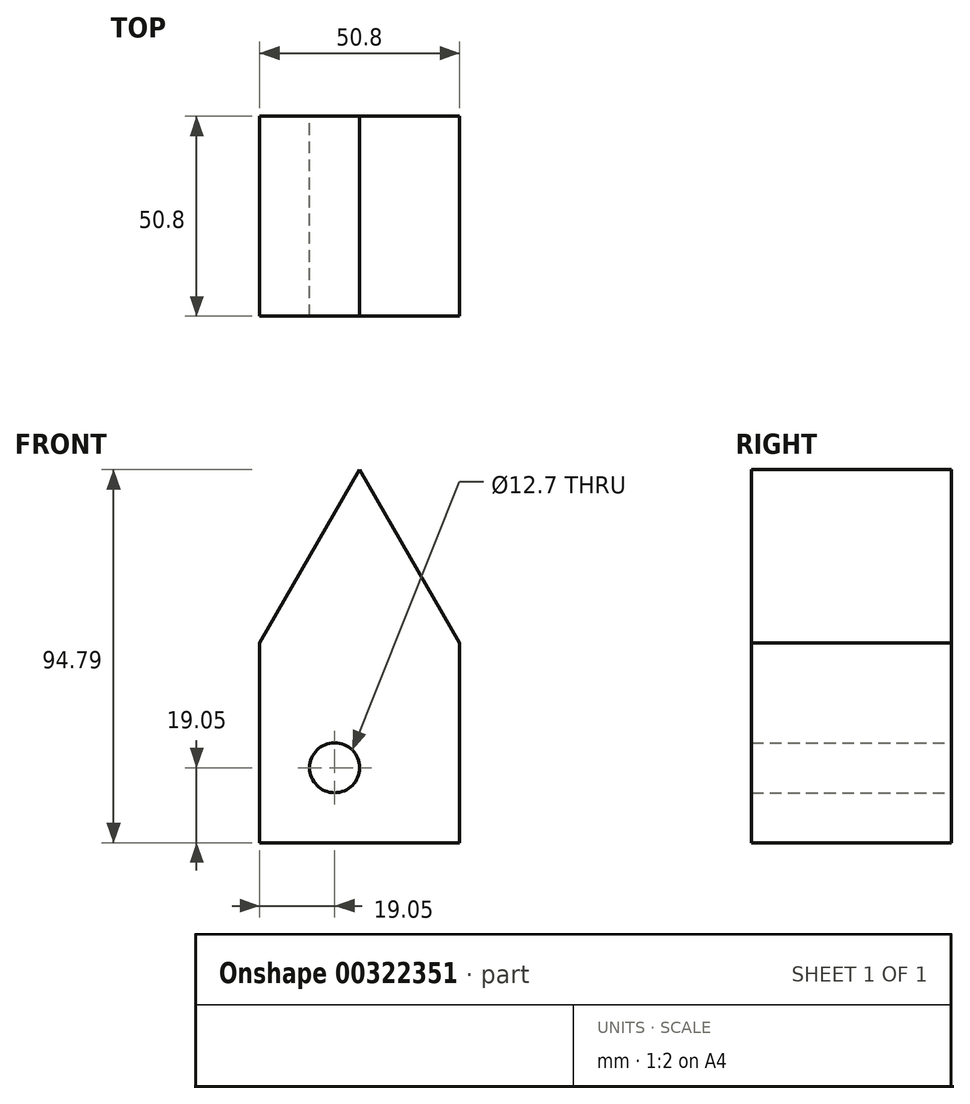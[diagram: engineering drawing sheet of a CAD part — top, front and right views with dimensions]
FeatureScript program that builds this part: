
annotation { "Feature Type Name" : "Feature", "Feature Type Description" : "" }
export const myFeature = defineFeature(function(context is Context, id is Id, definition is map)
    precondition{}
    {
        {
            var Q0;
            Q0=qCreatedBy(makeId("Front.planeOp"),FACE);
            var sketch = newSketch(context, id + "F0", { "sketchPlane" : qUnion([Q0])});
            skLineSegment(sketch, "E0.bottom", {"start": v(25.4, 25.4) * mm, "end": v(-25.4, 25.4) * mm});
            skLineSegment(sketch, "E0.top", {"start": v(25.4, -25.4) * mm, "end": v(-25.4, -25.4) * mm});
            skLineSegment(sketch, "E0.left", {"start": v(25.4, 25.4) * mm, "end": v(25.4, -25.4) * mm});
            skLineSegment(sketch, "E0.right", {"start": v(-25.4, 25.4) * mm, "end": v(-25.4, -25.4) * mm});
            skPoint(sketch, "E0.middle", {"position": v(0, 0) * mm});
            skLineSegment(sketch, "E1", {"start": v(-25.4, 25.4) * mm, "end": v(0, 69.4) * mm});
            skLineSegment(sketch, "E2", {"start": v(25.4, 25.4) * mm, "end": v(0, 69.4) * mm});
            skCircle(sketch, "E3", {"center": v(-6.35, -6.35) * mm, "radius": 6.35 * mm});
            skSolve(sketch);
        }
        {
            var Q0;
            {var subQ3=sQuery(id+"F0.wireOp",EDGE,"E1");Q0=makeQuery(id+"F0.imprint","IMPRINT",FACE,{"disambiguationData":[TD([[makeQuery(id+"F0.imprint","IMPRINT",EDGE,{"derivedFrom":subQ3}),-1.0]])]});}
            var Q1;
            {var subQ0=sQuery(id+"F0.wireOp",EDGE,"E0.right");var subQ5=sQuery(id+"F0.wireOp",EDGE,"e86970d0-9a30-4200-a62f-9d334c886f84.0");var subQ6=makeQuery(id+"F0.imprint","INTERSECT",VERTEX,{"derivedFrom":[subQ0,subQ5]});Q1=makeQuery(id+"F0.imprint","IMPRINT",FACE,{"disambiguationData":[TD([[makeQuery(id+"F0.imprint","IMPRINT",EDGE,{"disambiguationData":[TD([[subQ6,1.0]])],"derivedFrom":subQ5}),-1.0]])]});}
            var Q2;
            {var subQ0=sQuery(id+"F0.wireOp",EDGE,"E0.right");var subQ1=sQuery(id+"F0.wireOp",EDGE,"E0.top");var subQ2=makeQuery(id+"F0.imprint","INTERSECT",VERTEX,{"derivedFrom":[subQ1,subQ0]});Q2=makeQuery(id+"F0.imprint","IMPRINT",FACE,{"disambiguationData":[TD([[makeQuery(id+"F0.imprint","IMPRINT",EDGE,{"disambiguationData":[TD([[subQ2,1.0]])],"derivedFrom":subQ1}),-1.0]])]});}
            var Q3;
            {var subQ0=sQuery(id+"F0.wireOp",EDGE,"E0.left");var subQ1=sQuery(id+"F0.wireOp",EDGE,"E0.top");var subQ2=makeQuery(id+"F0.imprint","INTERSECT",VERTEX,{"derivedFrom":[subQ1,subQ0]});Q3=makeQuery(id+"F0.imprint","IMPRINT",FACE,{"disambiguationData":[TD([[makeQuery(id+"F0.imprint","IMPRINT",EDGE,{"disambiguationData":[TD([[subQ2,-1.0]])],"derivedFrom":subQ1}),-1.0]])]});}
            var Q4;
            {var subQ0=sQuery(id+"F0.wireOp",EDGE,"E0.left");var subQ5=sQuery(id+"F0.wireOp",EDGE,"e86970d0-9a30-4200-a62f-9d334c886f84.0");var subQ6=makeQuery(id+"F0.imprint","INTERSECT",VERTEX,{"derivedFrom":[subQ0,subQ5]});Q4=makeQuery(id+"F0.imprint","IMPRINT",FACE,{"disambiguationData":[TD([[makeQuery(id+"F0.imprint","IMPRINT",EDGE,{"disambiguationData":[TD([[subQ6,-1.0]])],"derivedFrom":subQ5}),-1.0]])]});}
            extrude(context, id + "F1", {"entities" : qUnion([Q0, Q1, Q2, Q3, Q4]), "depth" : 25.4 * mm});
        }
        {
            var Q0;
            Q0 = qSketchRegion(id + "F0", true);
            extrude(context, id + "F2", {"entities" : qUnion([Q0]), "operationType" : NewBodyOperationType.ADD, "depth" : 50.8 * mm});
        }
    });
